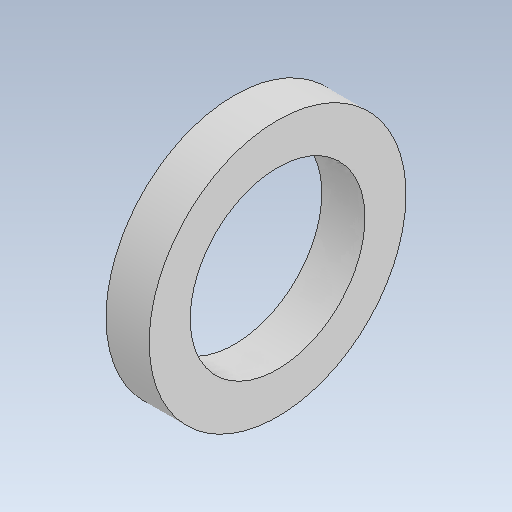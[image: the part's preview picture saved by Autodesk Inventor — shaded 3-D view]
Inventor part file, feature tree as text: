
AUTODESK INVENTOR PART (.ipt)
format: ipt  version: 2021 (Build 250183000, 183)  size: 112,128 bytes
history: native  units: mm
features: extrude x1, sketch x1
ambient origin geometry x8: Origin, YZ Plane, XZ Plane, XY Plane, X Axis, Y Axis, Z Axis, Center Point
bodies: Solid1 (feature_tree)
feature tree (2):
  extrude  "Extrusion1"  Depth=10.0mm
  sketch  "Sketch1"  dims[d0=40.5mm d1=9.5mm d2=10.0mm d3=0.0mm]
